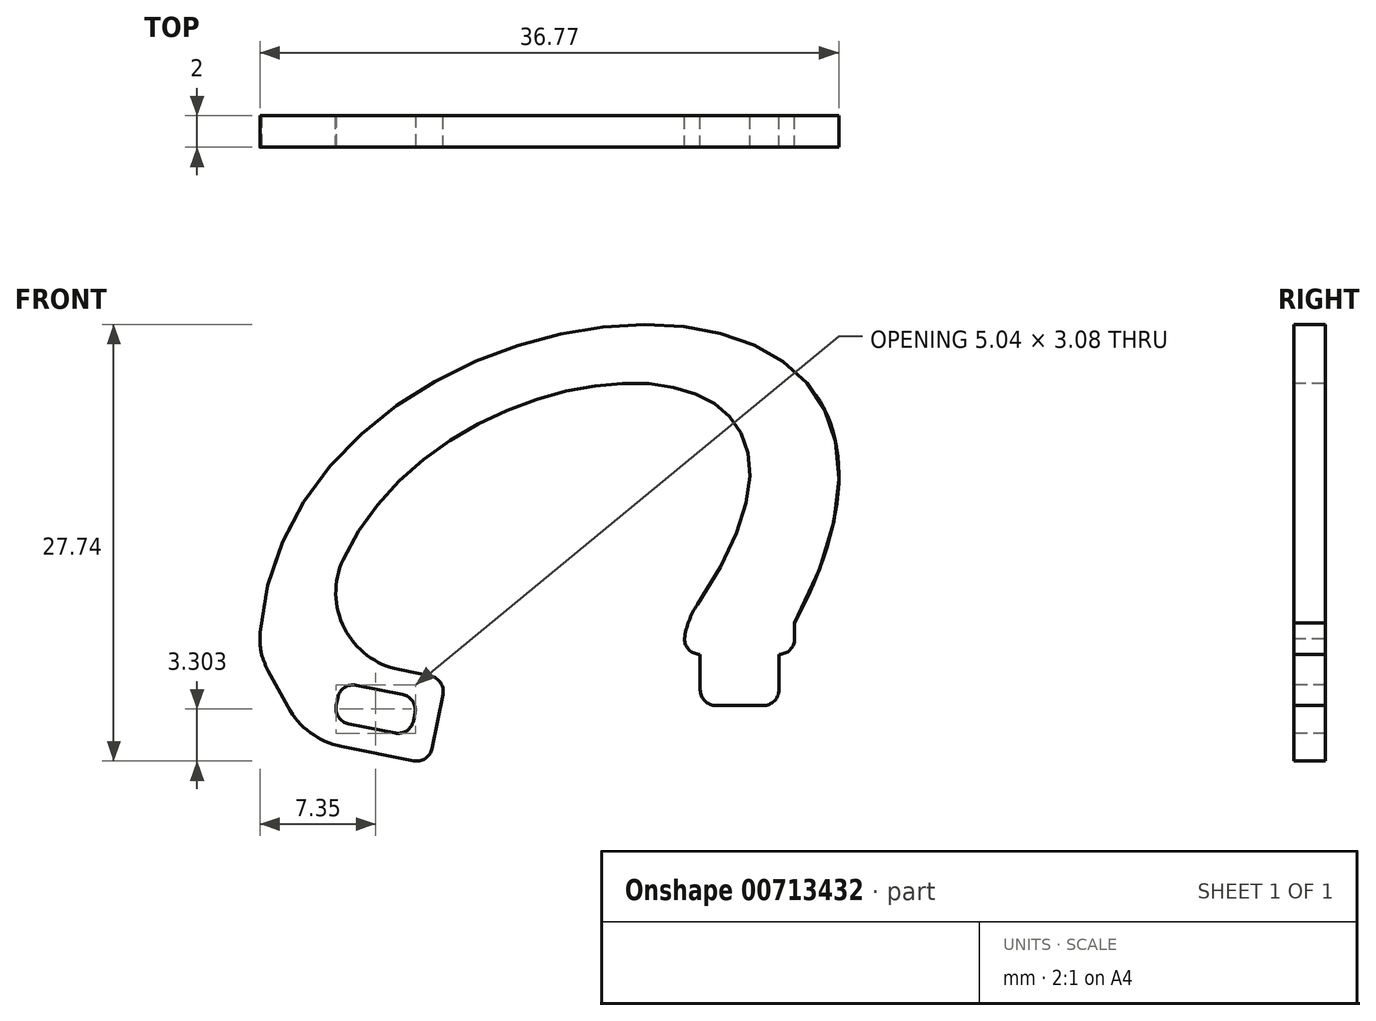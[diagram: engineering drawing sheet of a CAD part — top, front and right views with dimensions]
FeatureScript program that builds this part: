
annotation { "Feature Type Name" : "Feature", "Feature Type Description" : "" }
export const myFeature = defineFeature(function(context is Context, id is Id, definition is map)
    precondition{}
    {
        {
            var Q0;
            Q0=qCreatedBy(makeId("Front.planeOp"),FACE);
            var sketch = newSketch(context, id + "F0", { "sketchPlane" : qUnion([Q0])});
            skLineSegment(sketch, "E0", {"start": v(-7.85, 0) * mm, "end": v(0, -1.56) * mm});
            skLineSegment(sketch, "E1", {"start": v(0, -1.56) * mm, "end": v(-1.07, -6.96) * mm});
            skLineSegment(sketch, "E2", {"start": v(-1.07, -6.96) * mm, "end": v(-8.92, -5.4) * mm});
            skLineSegment(sketch, "E3", {"start": v(-8.92, -5.4) * mm, "end": v(-7.85, 0) * mm});
            skLineSegment(sketch, "E4.0", {"start": v(-6.67, -1.76) * mm, "end": v(-1.76, -2.74) * mm});
            skLineSegment(sketch, "E4.1", {"start": v(-7.16, -4.22) * mm, "end": v(-6.67, -1.76) * mm});
            skLineSegment(sketch, "E4.2", {"start": v(-2.25, -5.2) * mm, "end": v(-7.16, -4.22) * mm});
            skLineSegment(sketch, "E4.3", {"start": v(-1.76, -2.74) * mm, "end": v(-2.25, -5.2) * mm});
            skLineSegment(sketch, "E5", {"start": v(-8.92, -5.4) * mm, "end": v(-11.85, 0) * mm});
            skLineSegment(sketch, "E6.bottom", {"start": v(16.15, 0) * mm, "end": v(21.15, 0) * mm});
            skLineSegment(sketch, "E6.top", {"start": v(16.15, -3.25) * mm, "end": v(21.15, -3.25) * mm});
            skLineSegment(sketch, "E6.left", {"start": v(16.15, 0) * mm, "end": v(16.15, -3.25) * mm});
            skLineSegment(sketch, "E6.right", {"start": v(21.15, 0) * mm, "end": v(21.15, -3.25) * mm});
            skLineSegment(sketch, "E7.bottom", {"start": v(15.15, 2) * mm, "end": v(22.15, 2) * mm});
            skLineSegment(sketch, "E7.left", {"start": v(15.15, 2) * mm, "end": v(15.15, 0) * mm});
            skLineSegment(sketch, "E7.right", {"start": v(22.15, 2) * mm, "end": v(22.15, 0) * mm});
            skLineSegment(sketch, "E8", {"start": v(15.15, 0) * mm, "end": v(16.15, 0) * mm});
            skLineSegment(sketch, "E9", {"start": v(21.15, 0) * mm, "end": v(22.15, 0) * mm});
            skFitSpline(sketch, "E10", {"points": [v(-11.85, 0) * mm, v(22.15, 2) * mm], "startDerivative": vector(0, 75) * mm, "endDerivative": vector(-44.54, -84) * mm});
            skFitSpline(sketch, "E11", {"points": [v(-7.85, 0) * mm, v(15.15, 2) * mm], "startDerivative": vector(0, 60) * mm, "endDerivative": vector(-50.54, -69) * mm});
            skSolve(sketch);
        }
        {
            var Q0;
            Q0=makeQuery(id+"F0.imprint","IMPRINT",FACE,{"disambiguationData":[TD([[makeQuery(id+"F0.imprint","IMPRINT",EDGE,{"derivedFrom":sQuery(id+"F0.wireOp",EDGE,"E0")}),-1.0]])]});
            var Q1;
            Q1=makeQuery(id+"F0.imprint","IMPRINT",FACE,{"disambiguationData":[TD([[makeQuery(id+"F0.imprint","IMPRINT",EDGE,{"derivedFrom":sQuery(id+"F0.wireOp",EDGE,"E3")}),1.0]])]});
            var Q2;
            Q2=makeQuery(id+"F0.imprint","IMPRINT",FACE,{"disambiguationData":[TD([[makeQuery(id+"F0.imprint","IMPRINT",EDGE,{"derivedFrom":sQuery(id+"F0.wireOp",EDGE,"E6.bottom")}),1.0]])]});
            var Q3;
            Q3=makeQuery(id+"F0.imprint","IMPRINT",FACE,{"disambiguationData":[TD([[makeQuery(id+"F0.imprint","IMPRINT",EDGE,{"derivedFrom":sQuery(id+"F0.wireOp",EDGE,"E6.bottom")}),-1.0]])]});
            extrude(context, id + "F1", {"entities" : qUnion([Q0, Q1, Q2, Q3]), "depth" : 2 * mm, "offsetDistance" : 25 * mm});
        }
        {
            var Q0;
            Q0=makeQuery(id+"F1.opExtrude","SWEPT_EDGE",EDGE,{"disambiguationData":[OSD([sQuery(id+"F0.wireOp",EDGE,"E1"),sQuery(id+"F0.wireOp",EDGE,"E2")])]});
            var Q1;
            Q1=makeQuery(id+"F1.opExtrude","SWEPT_EDGE",EDGE,{"disambiguationData":[OSD([sQuery(id+"F0.wireOp",EDGE,"E0"),sQuery(id+"F0.wireOp",EDGE,"E1")])]});
            var Q2;
            Q2=makeQuery(id+"F1.opExtrude","SWEPT_EDGE",EDGE,{"disambiguationData":[OSD([sQuery(id+"F0.wireOp",EDGE,"E4.1"),sQuery(id+"F0.wireOp",EDGE,"E4.2")])]});
            var Q3;
            Q3=makeQuery(id+"F1.opExtrude","SWEPT_EDGE",EDGE,{"disambiguationData":[OSD([sQuery(id+"F0.wireOp",EDGE,"E4.0"),sQuery(id+"F0.wireOp",EDGE,"E4.1")])]});
            var Q4;
            Q4=makeQuery(id+"F1.opExtrude","SWEPT_EDGE",EDGE,{"disambiguationData":[OSD([sQuery(id+"F0.wireOp",EDGE,"E4.0"),sQuery(id+"F0.wireOp",EDGE,"E4.3")])]});
            var Q5;
            Q5=makeQuery(id+"F1.opExtrude","SWEPT_EDGE",EDGE,{"disambiguationData":[OSD([sQuery(id+"F0.wireOp",EDGE,"E4.2"),sQuery(id+"F0.wireOp",EDGE,"E4.3")])]});
            var Q6;
            Q6=makeQuery(id+"F1.opExtrude","SWEPT_EDGE",EDGE,{"disambiguationData":[OSD([sQuery(id+"F0.wireOp",EDGE,"E7.left"),sQuery(id+"F0.wireOp",EDGE,"E8")])]});
            var Q7;
            Q7=makeQuery(id+"F1.opExtrude","SWEPT_EDGE",EDGE,{"disambiguationData":[OSD([sQuery(id+"F0.wireOp",EDGE,"E7.right"),sQuery(id+"F0.wireOp",EDGE,"E9")])]});
            var Q8;
            Q8=makeQuery(id+"F1.opExtrude","SWEPT_EDGE",EDGE,{"disambiguationData":[OSD([sQuery(id+"F0.wireOp",EDGE,"E6.top"),sQuery(id+"F0.wireOp",EDGE,"E6.left")])]});
            var Q9;
            Q9=makeQuery(id+"F1.opExtrude","SWEPT_EDGE",EDGE,{"disambiguationData":[OSD([sQuery(id+"F0.wireOp",EDGE,"E6.top"),sQuery(id+"F0.wireOp",EDGE,"E6.right")])]});
            fillet(context, id + "F2", {"entities" : qUnion([Q0, Q1, Q2, Q3, Q4, Q5, Q6, Q7, Q8, Q9]), "radius" : 1 * mm, "tangentPropagation" : true, "allowEdgeOverflow" : false});
        }
        {
            var Q0;
            Q0=makeQuery(id+"F1.opExtrude","SWEPT_EDGE",EDGE,{"disambiguationData":[OSD([sQuery(id+"F0.wireOp",EDGE,"E5"),sQuery(id+"F0.wireOp",EDGE,"E10")])]});
            chamfer(context, id + "F3", {"entities" : qUnion([Q0]), "width" : 2 * mm, "tangentPropagation" : true});
        }
        {
            var Q0;
            Q0=makeQuery(id+"F1.opExtrude","SWEPT_EDGE",EDGE,{"disambiguationData":[OSD([sQuery(id+"F0.wireOp",EDGE,"E0"),sQuery(id+"F0.wireOp",EDGE,"E3"),sQuery(id+"F0.wireOp",EDGE,"E11")])]});
            var Q1;
            {var subQ0=sQuery(id+"F0.wireOp",EDGE,"E5");Q1=makeQuery(id+"F3.opChamfer","BLEND_EDGE",EDGE,{"blendedFrom":[makeQuery(id+"F1.opExtrude","SWEPT_EDGE",EDGE,{"disambiguationData":[OSD([subQ0,sQuery(id+"F0.wireOp",EDGE,"E10")])]}),makeQuery(id+"F1.opExtrude","SWEPT_FACE",FACE,{"disambiguationData":[OSD([subQ0])]})],"blendedInto":[makeQuery(id+"F1.opExtrude","SWEPT_FACE",FACE,{"disambiguationData":[OSD([subQ0])]})]});}
            var Q2;
            Q2=makeQuery(id+"F1.opExtrude","SWEPT_EDGE",EDGE,{"disambiguationData":[OSD([sQuery(id+"F0.wireOp",EDGE,"E2"),sQuery(id+"F0.wireOp",EDGE,"E3"),sQuery(id+"F0.wireOp",EDGE,"E5")])]});
            var Q3;
            {var subQ0=sQuery(id+"F0.wireOp",EDGE,"E10");Q3=makeQuery(id+"F3.opChamfer","BLEND_EDGE",EDGE,{"blendedFrom":[makeQuery(id+"F1.opExtrude","SWEPT_EDGE",EDGE,{"disambiguationData":[OSD([sQuery(id+"F0.wireOp",EDGE,"E5"),subQ0])]}),makeQuery(id+"F1.opExtrude","SWEPT_FACE",FACE,{"disambiguationData":[OSD([subQ0])]})],"blendedInto":[makeQuery(id+"F1.opExtrude","SWEPT_FACE",FACE,{"disambiguationData":[OSD([subQ0])]})]});}
            var Q4;
            Q4=makeQuery(id+"F1.opExtrude","SWEPT_EDGE",EDGE,{"disambiguationData":[OSD([sQuery(id+"F0.wireOp",EDGE,"E7.bottom"),sQuery(id+"F0.wireOp",EDGE,"E7.left"),sQuery(id+"F0.wireOp",EDGE,"E11")])]});
            fillet(context, id + "F4", {"entities" : qUnion([Q0, Q1, Q2, Q3, Q4]), "radius" : 5 * mm, "tangentPropagation" : true, "allowEdgeOverflow" : false});
        }
    });
